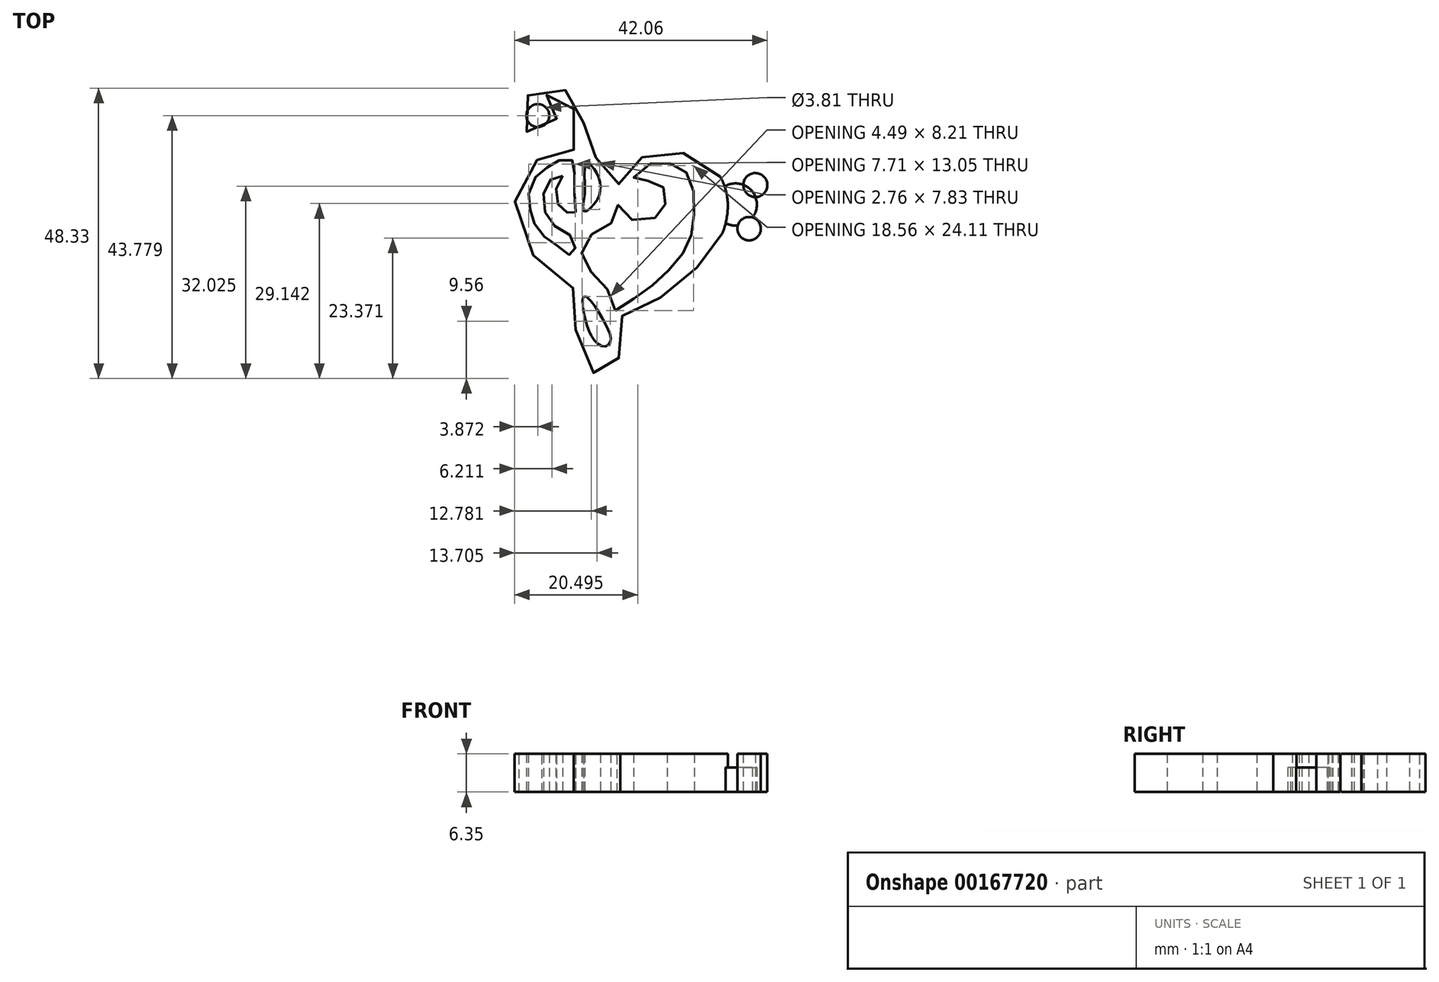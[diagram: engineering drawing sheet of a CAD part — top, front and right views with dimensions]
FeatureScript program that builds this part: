
annotation { "Feature Type Name" : "Feature", "Feature Type Description" : "" }
export const myFeature = defineFeature(function(context is Context, id is Id, definition is map)
    precondition{}
    {
        {
            var Q0;
            Q0=qCreatedBy(makeId("Top.planeOp"),FACE);
            var sketch = newSketch(context, id + "F0", { "sketchPlane" : qUnion([Q0])});
            skFitSpline(sketch, "E0", {"points": [v(-13.07, 11.62) * mm, v(-13.03, 14.61) * mm, v(-13.2, 18.03) * mm, v(-14, 19.74) * mm, v(-16.06, 20.73) * mm, v(-17.44, 20.73) * mm, v(-18.51, 20.23) * mm, v(-17.23, 19.63) * mm, v(-16.23, 17.64) * mm, v(-16.45, 14.86) * mm, v(-19, 13.83) * mm, v(-21.54, 14.97) * mm, v(-22.32, 17.81) * mm, v(-21.29, 20.23) * mm, v(-19.8, 21.23) * mm, v(-18.9, 21.59) * mm, v(-14.81, 21.48) * mm, v(-12.28, 19.6) * mm, v(-11.79, 17.6) * mm, v(-11.54, 14.36) * mm, v(-11.35, 11.48) * mm, v(-9.72, 10.27) * mm, v(-7.09, 7.57) * mm, v(-6.17, 5.6) * mm, v(-5.86, 5.65) * mm, v(-5.3, 7.21) * mm, v(-4.06, 8.95) * mm, v(-1.64, 10.34) * mm, v(1.24, 10.98) * mm, v(4.08, 11.09) * mm, v(7.14, 10.34) * mm, v(10.13, 8.24) * mm, v(11.66, 5.9) * mm, v(12.34, 3.01) * mm, v(12.16, 0.02) * mm, v(11.2, -2.97) * mm, v(9.39, -5.6) * mm, v(7.57, -7.73) * mm, v(4.97, -10.15) * mm, v(1.91, -12.6) * mm, v(-0.76, -14.2) * mm, v(-3.32, -15.53) * mm, v(-5.88, -16.66) * mm, v(-5.67, -19.2) * mm, v(-5.84, -23.53) * mm, v(-7.34, -26.34) * mm, v(-9.12, -26.34) * mm, v(-10.72, -24.6) * mm, v(-12.25, -21.43) * mm, v(-13.14, -16.77) * mm, v(-13.17, -13.04) * mm, v(-13.14, -11.83) * mm, v(-16.23, -9.44) * mm, v(-19.54, -6.6) * mm, v(-22.64, -1.33) * mm, v(-23, 3.4) * mm, v(-21.96, 6.43) * mm, v(-19.19, 9.95) * mm, v(-16.55, 11.13) * mm, v(-13.92, 11.59) * mm, v(-13.07, 11.62) * mm]});
            skFitSpline(sketch, "E1", {"points": [v(-11.65, -12.9) * mm, v(-11.54, -15.78) * mm, v(-10.74, -18.61) * mm, v(-9.41, -20.64) * mm, v(-8.13, -21.22) * mm, v(-7.28, -20.69) * mm, v(-7.17, -19.52) * mm, v(-7.97, -17.6) * mm, v(-10.16, -13.97) * mm, v(-11.65, -12.9) * mm]});
            skFitSpline(sketch, "E2", {"points": [v(-6.32, -15.25) * mm, v(-7.39, -12.37) * mm, v(-10, -9.07) * mm, v(-11.5, -7.79) * mm, v(-11.54, -3.36) * mm, v(-9.25, -2.3) * mm, v(-6.7, -0.06) * mm, v(-5.95, 2.34) * mm, v(-4.67, 0.48) * mm, v(-1.26, -0.27) * mm, v(1.14, 0.85) * mm, v(2, 2.55) * mm, v(2.16, 4.58) * mm, v(0.66, 5.86) * mm, v(-0.88, 6.34) * mm, v(-3.17, 6.34) * mm, v(-2.7, 7.89) * mm, v(0.61, 9.49) * mm, v(2.9, 9.17) * mm, v(4.82, 8.41) * mm, v(6.15, 6.47) * mm, v(6.76, 3.68) * mm, v(6.69, 0) * mm, v(6.32, -2.5) * mm, v(5.4, -4.9) * mm, v(3.54, -7.36) * mm, v(1.37, -9.7) * mm, v(-0.96, -11.65) * mm, v(-3.92, -13.79) * mm, v(-6.32, -15.25) * mm]});
            skCircle(sketch, "E3", {"center": v(16.95, 5.64) * mm, "radius": 2 * mm});
            skCircle(sketch, "E4", {"center": v(15.91, -1.63) * mm, "radius": 1.95 * mm});
            skFitSpline(sketch, "E5", {"points": [v(-11.21, 9.37) * mm, v(-11.41, 4.46) * mm, v(-11.53, 3.58) * mm, v(-11.57, 1.26) * mm, v(-9.72, 2.66) * mm, v(-8.86, 4.7) * mm, v(-9.18, 7.1) * mm, v(-10.41, 8.97) * mm, v(-11.21, 9.37) * mm]});
            skFitSpline(sketch, "E6", {"points": [v(-15.13, 7.17) * mm, v(-16.05, 5.46) * mm, v(-16, 2.82) * mm, v(-15.13, 1.5) * mm, v(-13.77, 0.82) * mm, v(-13.1, 0.86) * mm, v(-13.1, 3.46) * mm, v(-13.13, 7.65) * mm, v(-13.37, 9.6) * mm, v(-14.37, 9.93) * mm, v(-16.55, 9.41) * mm, v(-18.08, 8.3) * mm, v(-19.84, 6.73) * mm, v(-20.8, 3.54) * mm, v(-20.44, 1.3) * mm, v(-19.8, -0.77) * mm, v(-18.2, -2.93) * mm, v(-16.13, -4.37) * mm, v(-14.29, -5.73) * mm, v(-13.33, -6.2) * mm, v(-13.21, -3.21) * mm, v(-14.29, -2.53) * mm, v(-17.2, -0.38) * mm, v(-18.16, 1.86) * mm, v(-18.04, 5.34) * mm, v(-16.55, 6.9) * mm, v(-15.13, 7.17) * mm]});
            skArc(sketch, "E7", {"start": v(12, -0.7) * mm, "mid": v(17.2, 2.49) * mm, "end": v(11.85, 5.4) * mm});
            skArc(sketch, "E8", {"start": v(11.46, -2.41) * mm, "mid": v(18.97, 2.6) * mm, "end": v(11.1, 7.02) * mm});
            skCircle(sketch, "E9", {"center": v(-19.24, 17.2) * mm, "radius": 1.9 * mm});
            skSolve(sketch);
        }
        {
            var Q0;
            Q0=makeQuery(id+"F0.imprint","IMPRINT",FACE,{"disambiguationData":[TD([[makeQuery(id+"F0.imprint","IMPRINT",EDGE,{"derivedFrom":sQuery(id+"F0.wireOp",EDGE,"E1")}),-1.0]])]});
            var Q1;
            {var subQ0=sQuery(id+"F0.wireOp",EDGE,"E8");var subQ1=sQuery(id+"F0.wireOp",EDGE,"E3");var subQ2=makeQuery(id+"F0.imprint","INTERSECT",VERTEX,{"disambiguationData":[OD(0.0)],"derivedFrom":[subQ1,subQ0]});Q1=makeQuery(id+"F0.imprint","IMPRINT",FACE,{"disambiguationData":[TD([[makeQuery(id+"F0.imprint","IMPRINT",EDGE,{"disambiguationData":[TD([[subQ2,1.0]])],"derivedFrom":subQ1}),1.0]])]});}
            var Q2;
            {var subQ0=sQuery(id+"F0.wireOp",EDGE,"E8");var subQ1=sQuery(id+"F0.wireOp",EDGE,"E3");var subQ2=makeQuery(id+"F0.imprint","INTERSECT",VERTEX,{"disambiguationData":[OD(0.0)],"derivedFrom":[subQ1,subQ0]});Q2=makeQuery(id+"F0.imprint","IMPRINT",FACE,{"disambiguationData":[TD([[makeQuery(id+"F0.imprint","IMPRINT",EDGE,{"disambiguationData":[TD([[subQ2,-1.0]])],"derivedFrom":subQ1}),1.0]])]});}
            var Q3;
            {var subQ0=sQuery(id+"F0.wireOp",EDGE,"E7");var subQ1=sQuery(id+"F0.wireOp",EDGE,"E3");var subQ2=makeQuery(id+"F0.imprint","INTERSECT",VERTEX,{"disambiguationData":[OD(0.0)],"derivedFrom":[subQ1,subQ0]});Q3=makeQuery(id+"F0.imprint","IMPRINT",FACE,{"disambiguationData":[TD([[makeQuery(id+"F0.imprint","IMPRINT",EDGE,{"disambiguationData":[TD([[subQ2,-1.0]])],"derivedFrom":subQ1}),1.0]])]});}
            var Q4;
            {var subQ0=sQuery(id+"F0.wireOp",EDGE,"E8");var subQ1=sQuery(id+"F0.wireOp",EDGE,"E4");var subQ2=makeQuery(id+"F0.imprint","INTERSECT",VERTEX,{"disambiguationData":[OD(0.0)],"derivedFrom":[subQ1,subQ0]});Q4=makeQuery(id+"F0.imprint","IMPRINT",FACE,{"disambiguationData":[TD([[makeQuery(id+"F0.imprint","IMPRINT",EDGE,{"disambiguationData":[TD([[subQ2,1.0]])],"derivedFrom":subQ1}),1.0]])]});}
            var Q5;
            {var subQ0=sQuery(id+"F0.wireOp",EDGE,"E8");var subQ1=sQuery(id+"F0.wireOp",EDGE,"E4");var subQ2=makeQuery(id+"F0.imprint","INTERSECT",VERTEX,{"disambiguationData":[OD(0.0)],"derivedFrom":[subQ1,subQ0]});Q5=makeQuery(id+"F0.imprint","IMPRINT",FACE,{"disambiguationData":[TD([[makeQuery(id+"F0.imprint","IMPRINT",EDGE,{"disambiguationData":[TD([[subQ2,-1.0]])],"derivedFrom":subQ1}),1.0]])]});}
            var Q6;
            {var subQ0=sQuery(id+"F0.wireOp",EDGE,"E7");var subQ1=sQuery(id+"F0.wireOp",EDGE,"E4");var subQ2=makeQuery(id+"F0.imprint","INTERSECT",VERTEX,{"disambiguationData":[OD(0.0)],"derivedFrom":[subQ1,subQ0]});Q6=makeQuery(id+"F0.imprint","IMPRINT",FACE,{"disambiguationData":[TD([[makeQuery(id+"F0.imprint","IMPRINT",EDGE,{"disambiguationData":[TD([[subQ2,-1.0]])],"derivedFrom":subQ1}),1.0]])]});}
            extrude(context, id + "F1", {"entities" : qUnion([Q0, Q1, Q2, Q3, Q4, Q5, Q6]), "depth" : 6.35 * mm});
        }
        {
            var Q0;
            {var subQ0=sQuery(id+"F0.wireOp",EDGE,"E7");var subQ1=sQuery(id+"F0.wireOp",EDGE,"E0");var subQ2=makeQuery(id+"F0.imprint","INTERSECT",VERTEX,{"disambiguationData":[OD(1.0)],"derivedFrom":[subQ1,subQ0]});Q0=makeQuery(id+"F0.imprint","IMPRINT",FACE,{"disambiguationData":[TD([[makeQuery(id+"F0.imprint","IMPRINT",EDGE,{"disambiguationData":[TD([[subQ2,1.0]])],"derivedFrom":subQ1}),1.0]])]});}
            var Q1;
            {var subQ0=sQuery(id+"F0.wireOp",EDGE,"E8");var subQ1=sQuery(id+"F0.wireOp",EDGE,"E3");var subQ2=makeQuery(id+"F0.imprint","INTERSECT",VERTEX,{"disambiguationData":[OD(1.0)],"derivedFrom":[subQ1,subQ0]});Q1=makeQuery(id+"F0.imprint","IMPRINT",FACE,{"disambiguationData":[TD([[makeQuery(id+"F0.imprint","IMPRINT",EDGE,{"disambiguationData":[TD([[subQ2,1.0]])],"derivedFrom":subQ1}),-1.0]])]});}
            var Q2;
            {var subQ0=sQuery(id+"F0.wireOp",EDGE,"E7");var subQ1=sQuery(id+"F0.wireOp",EDGE,"E0");var subQ2=makeQuery(id+"F0.imprint","INTERSECT",VERTEX,{"disambiguationData":[OD(0.0)],"derivedFrom":[subQ1,subQ0]});Q2=makeQuery(id+"F0.imprint","IMPRINT",FACE,{"disambiguationData":[TD([[makeQuery(id+"F0.imprint","IMPRINT",EDGE,{"disambiguationData":[TD([[subQ2,-1.0]])],"derivedFrom":subQ1}),1.0]])]});}
            extrude(context, id + "F2", {"entities" : qUnion([Q0, Q1, Q2]), "operationType" : NewBodyOperationType.ADD, "depth" : 4.06 * mm});
        }
    });
